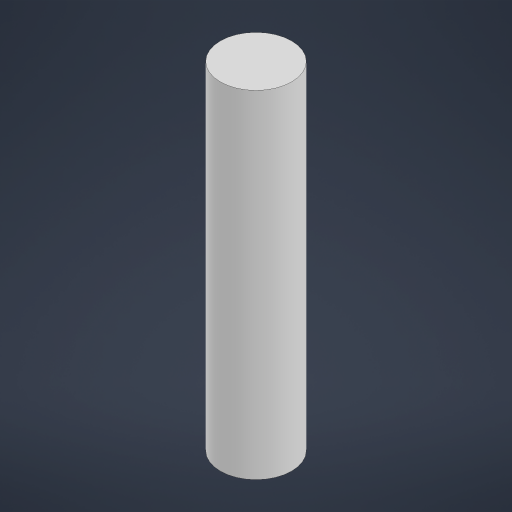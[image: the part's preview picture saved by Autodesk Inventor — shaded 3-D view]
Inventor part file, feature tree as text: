
AUTODESK INVENTOR PART (.ipt)
format: ipt  version: 2023 (Build 270158000, 158)  size: 141,824 bytes
history: native  units: in
note: dims shown in document units (in); Inventor stores cm internally (conversion verified against a paired STEP export)
features: extrude x1, sketch x1
ambient origin geometry x8: Origin, YZ Plane, XZ Plane, XY Plane, X Axis, Y Axis, Z Axis, Center Point
bodies: Solid1 (feature_tree)
feature tree (2):
  extrude  "Extrusion1"  Depth=0.7087in TaperAngle=0.0deg
  sketch  "Sketch1"  dims[d0=0.1496in d1=0.7087in d2=0.0in]
